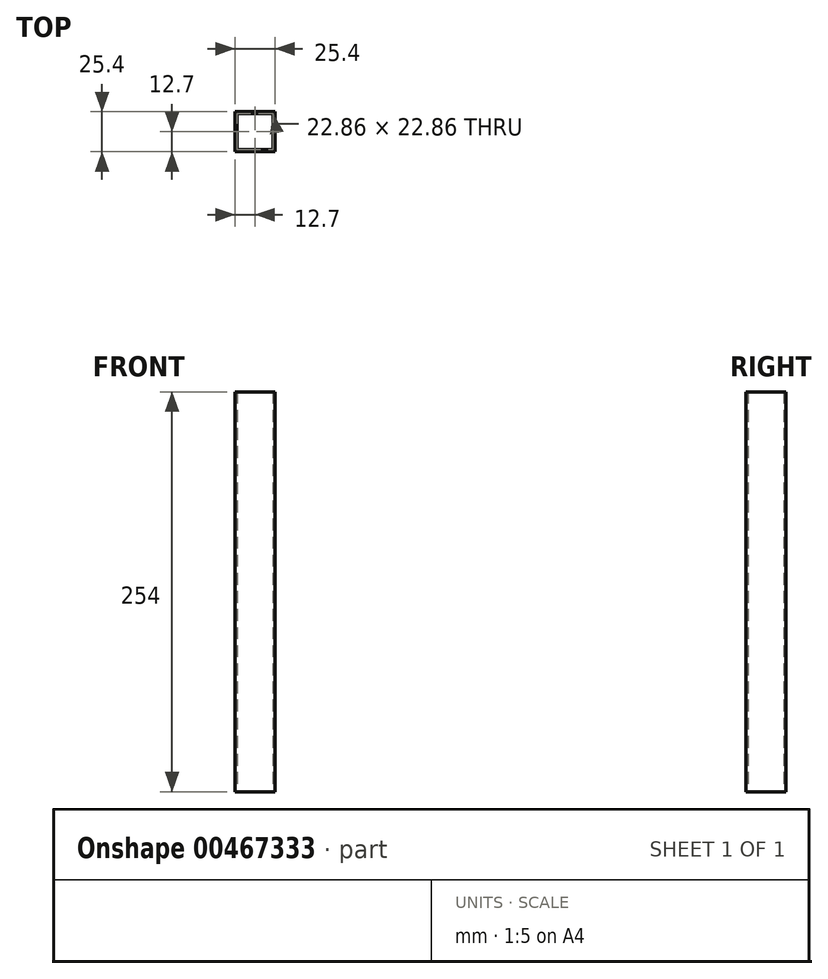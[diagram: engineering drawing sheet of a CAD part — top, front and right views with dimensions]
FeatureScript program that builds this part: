
annotation { "Feature Type Name" : "Feature", "Feature Type Description" : "" }
export const myFeature = defineFeature(function(context is Context, id is Id, definition is map)
    precondition{}
    {
        {
            var Q0;
            Q0=qCreatedBy(makeId("Top.planeOp"),FACE);
            var sketch = newSketch(context, id + "F0", { "sketchPlane" : qUnion([Q0])});
            skLineSegment(sketch, "E0.bottom", {"start": v(-12.7, 12.7) * mm, "end": v(12.7, 12.7) * mm});
            skLineSegment(sketch, "E0.top", {"start": v(-12.7, -12.7) * mm, "end": v(12.7, -12.7) * mm});
            skLineSegment(sketch, "E0.left", {"start": v(-12.7, 12.7) * mm, "end": v(-12.7, -12.7) * mm});
            skLineSegment(sketch, "E0.right", {"start": v(12.7, 12.7) * mm, "end": v(12.7, -12.7) * mm});
            skPoint(sketch, "E0.middle", {"position": v(0, 0) * mm});
            skLineSegment(sketch, "E1.0", {"start": v(-11.43, 11.43) * mm, "end": v(-11.43, -11.43) * mm});
            skLineSegment(sketch, "E1.1", {"start": v(-11.43, 11.43) * mm, "end": v(11.43, 11.43) * mm});
            skLineSegment(sketch, "E1.2", {"start": v(11.43, 11.43) * mm, "end": v(11.43, -11.43) * mm});
            skLineSegment(sketch, "E1.3", {"start": v(-11.43, -11.43) * mm, "end": v(11.43, -11.43) * mm});
            skSolve(sketch);
        }
        {
            var Q0;
            Q0=makeQuery(id+"F0.imprint","IMPRINT",FACE,{"disambiguationData":[TD([[makeQuery(id+"F0.imprint","IMPRINT",EDGE,{"derivedFrom":sQuery(id+"F0.wireOp",EDGE,"E0.bottom")}),-1.0]])]});
            extrude(context, id + "F1", {"entities" : qUnion([Q0]), "depth" : 254 * mm});
        }
    });
